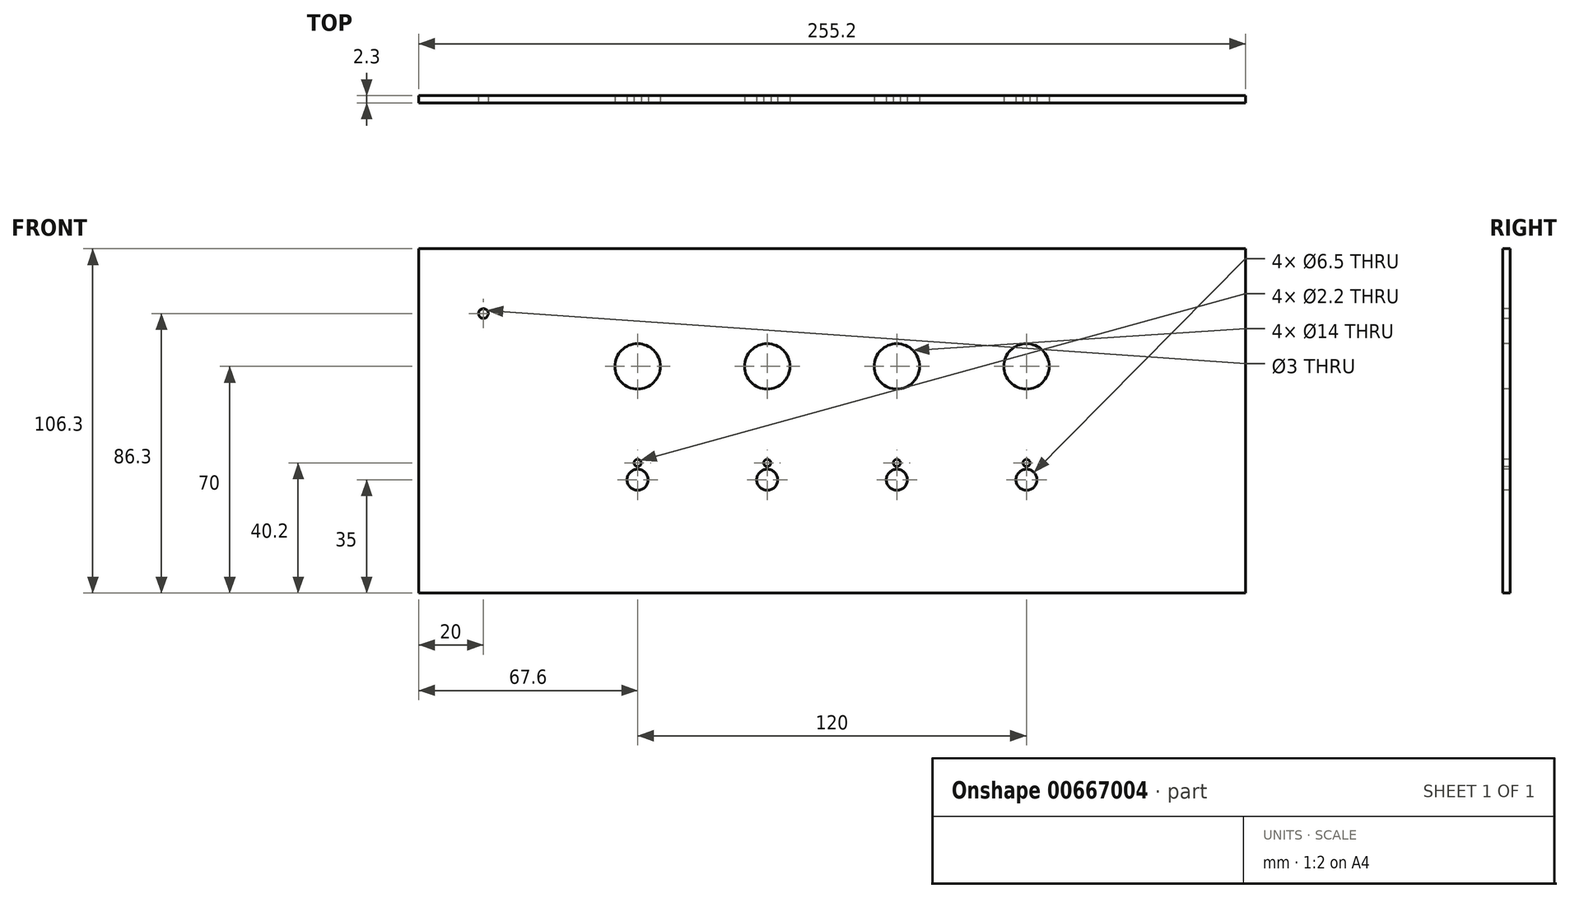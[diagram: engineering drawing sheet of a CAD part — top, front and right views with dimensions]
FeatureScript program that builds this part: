
annotation { "Feature Type Name" : "Feature", "Feature Type Description" : "" }
export const myFeature = defineFeature(function(context is Context, id is Id, definition is map)
    precondition{}
    {
        {
            var Q0;
            Q0=qCreatedBy(makeId("Front.planeOp"),FACE);
            var sketch = newSketch(context, id + "F0", { "sketchPlane" : qUnion([Q0])});
            skLineSegment(sketch, "E0.bottom", {"start": v(127.6, -53.15) * mm, "end": v(-127.6, -53.15) * mm});
            skLineSegment(sketch, "E0.top", {"start": v(127.6, 53.15) * mm, "end": v(-127.6, 53.15) * mm});
            skLineSegment(sketch, "E0.left", {"start": v(127.6, -53.15) * mm, "end": v(127.6, 53.15) * mm});
            skLineSegment(sketch, "E0.right", {"start": v(-127.6, -53.15) * mm, "end": v(-127.6, 53.15) * mm});
            skPoint(sketch, "E0.middle", {"position": v(0, 0) * mm});
            skCircle(sketch, "E1", {"center": v(-107.6, 33.15) * mm, "radius": 1.5 * mm});
            skCircle(sketch, "E2", {"center": v(-60, -18.15) * mm, "radius": 3.25 * mm});
            skCircle(sketch, "E3", {"center": v(-60, -12.95) * mm, "radius": 1.1 * mm});
            skCircle(sketch, "E4.1.0.0", {"center": v(-20, -18.15) * mm, "radius": 3.25 * mm});
            skCircle(sketch, "E4.2.0.0", {"center": v(20, -18.15) * mm, "radius": 3.25 * mm});
            skCircle(sketch, "E4.3.0.0", {"center": v(60, -18.15) * mm, "radius": 3.25 * mm});
            skLineSegment(sketch, "E4.direction1", {"start": v(-60, -18.15) * mm, "end": v(-20, -18.15) * mm, "construction": true});
            skCircle(sketch, "E5.1.0.0", {"center": v(-20, -12.95) * mm, "radius": 1.1 * mm});
            skCircle(sketch, "E5.2.0.0", {"center": v(20, -12.95) * mm, "radius": 1.1 * mm});
            skCircle(sketch, "E5.3.0.0", {"center": v(60, -12.95) * mm, "radius": 1.1 * mm});
            skLineSegment(sketch, "E5.direction1", {"start": v(-60, -12.95) * mm, "end": v(-20, -12.95) * mm, "construction": true});
            skCircle(sketch, "E6", {"center": v(-60, 16.85) * mm, "radius": 7 * mm});
            skCircle(sketch, "E7.1.0.0", {"center": v(-20, 16.85) * mm, "radius": 7 * mm});
            skCircle(sketch, "E7.2.0.0", {"center": v(20, 16.85) * mm, "radius": 7 * mm});
            skCircle(sketch, "E7.3.0.0", {"center": v(60, 16.85) * mm, "radius": 7 * mm});
            skLineSegment(sketch, "E7.direction1", {"start": v(-60, 16.85) * mm, "end": v(-20, 16.85) * mm, "construction": true});
            skSolve(sketch);
        }
        {
            var Q0;
            Q0=makeQuery(id+"F0.imprint","IMPRINT",FACE,{"disambiguationData":[TD([[makeQuery(id+"F0.imprint","IMPRINT",EDGE,{"derivedFrom":sQuery(id+"F0.wireOp",EDGE,"E0.bottom")}),-1.0]])]});
            extrude(context, id + "F1", {"entities" : qUnion([Q0]), "oppositeDirection" : true, "depth" : 2.3 * mm, "offsetDistance" : 25 * mm});
        }
    });
